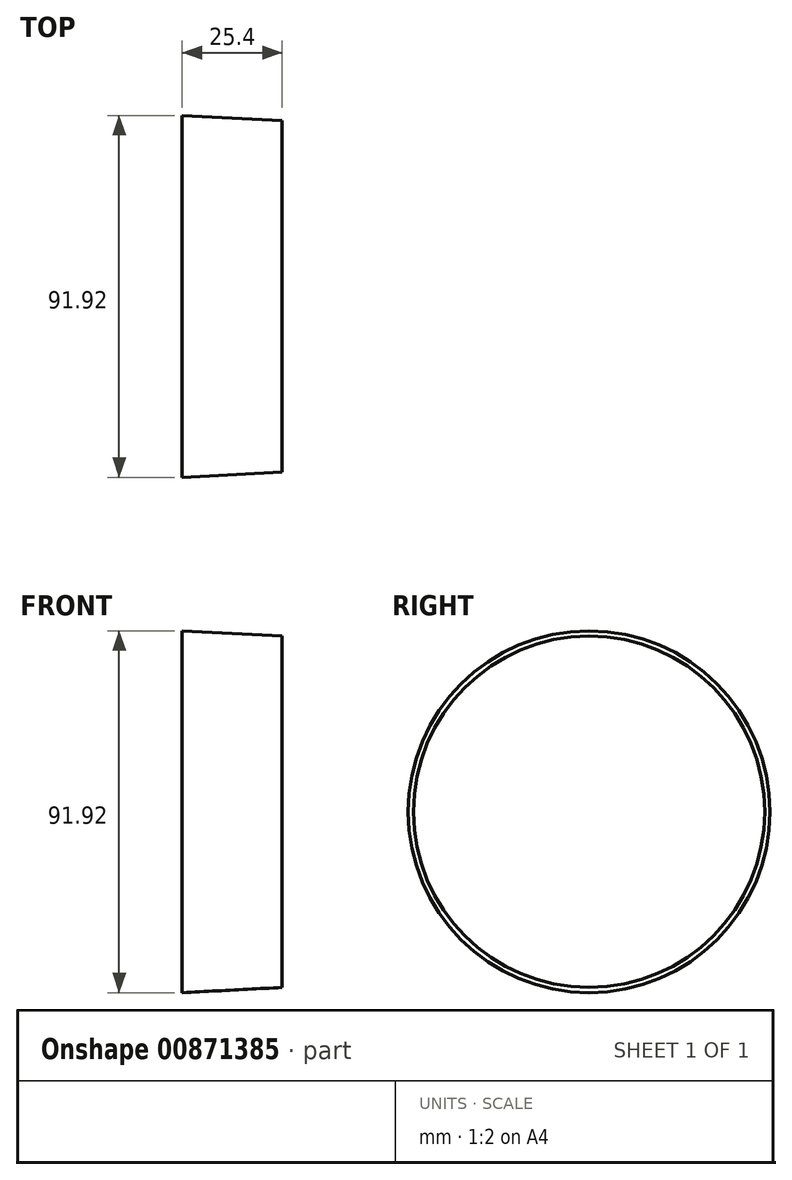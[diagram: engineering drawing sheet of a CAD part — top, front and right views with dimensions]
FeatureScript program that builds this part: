
annotation { "Feature Type Name" : "Feature", "Feature Type Description" : "" }
export const myFeature = defineFeature(function(context is Context, id is Id, definition is map)
    precondition{}
    {
        {
            var Q0;
            Q0=qCreatedBy(makeId("Right.planeOp"),FACE);
            var sketch = newSketch(context, id + "F0", { "sketchPlane" : qUnion([Q0])});
            skCircle(sketch, "E0", {"center": v(-44.62, 40.85) * mm, "radius": 44.63 * mm});
            skPoint(sketch, "E0.first.point", {"position": v(0, 41.65) * mm});
            skPoint(sketch, "E0.second.point", {"position": v(0, 40.05) * mm});
            skPoint(sketch, "E0.third.point", {"position": v(-88.28, 50.1) * mm});
            skSolve(sketch);
        }
        {
            var Q0;
            Q0=makeQuery(id+"F0.imprint","IMPRINT",FACE,{"disambiguationData":[TD([[makeQuery(id+"F0.imprint","IMPRINT",EDGE,{"derivedFrom":sQuery(id+"F0.wireOp",EDGE,"E0")}),1.0]])]});
            extrude(context, id + "F1", {"entities" : qUnion([Q0]), "oppositeDirection" : true, "depth" : 25.4 * mm, "offsetDistance" : 25.4 * mm, "hasDraft" : true, "draftAngle" : 3 * degree});
        }
    });
